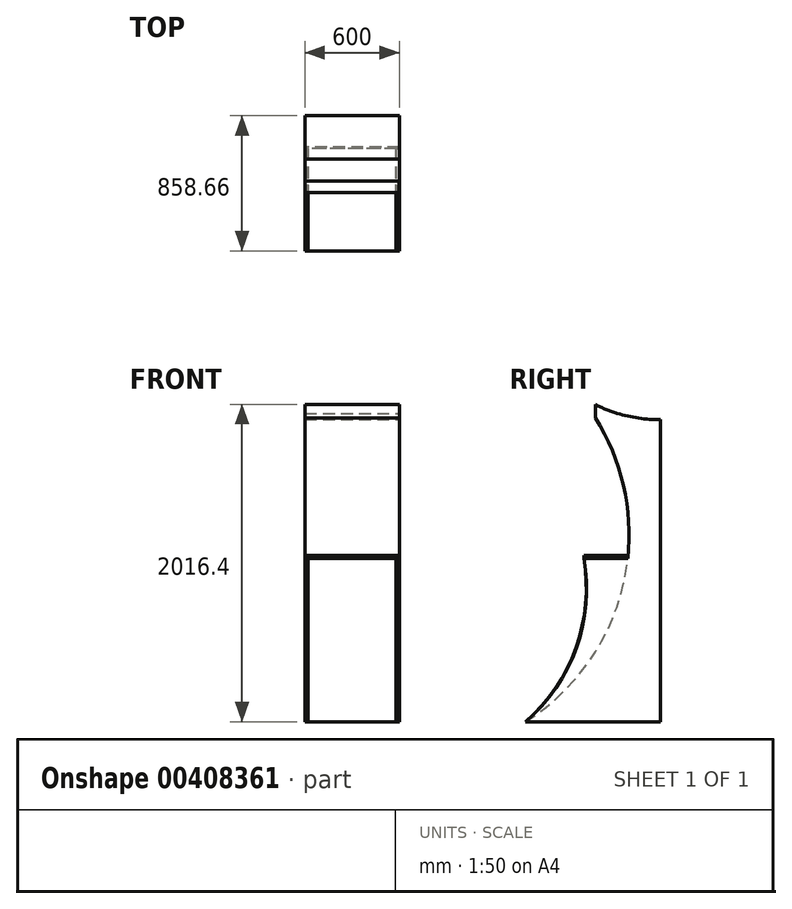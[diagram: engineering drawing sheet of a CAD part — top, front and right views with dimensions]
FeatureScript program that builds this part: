
annotation { "Feature Type Name" : "Feature", "Feature Type Description" : "" }
export const myFeature = defineFeature(function(context is Context, id is Id, definition is map)
    precondition{}
    {
        {
            var Q0;
            Q0=qCreatedBy(makeId("Right.planeOp"),FACE);
            var sketch = newSketch(context, id + "F0", { "sketchPlane" : qUnion([Q0])});
            skLineSegment(sketch, "E0", {"start": v(-858.66, 1.3) * mm, "end": v(841.34, 1.3) * mm});
            skPoint(sketch, "E1.end.orphan", {"position": v(0, 1171.1) * mm});
            skArc(sketch, "E2", {"start": v(-413.77, 2017.7) * mm, "mid": v(-217.07, 1948.77) * mm, "end": v(-8.66, 1951.3) * mm});
            skArc(sketch, "E3", {"start": v(-8.66, 1951.3) * mm, "mid": v(199.75, 1948.77) * mm, "end": v(396.44, 2017.7) * mm});
            skLineSegment(sketch, "E4", {"start": v(-413.77, 2017.7) * mm, "end": v(-413.77, 1932.7) * mm});
            skLineSegment(sketch, "E5", {"start": v(396.44, 2017.7) * mm, "end": v(396.44, 1932.7) * mm});
            skArc(sketch, "E6", {"start": v(-858.66, 1.3) * mm, "mid": v(-235.62, 874.72) * mm, "end": v(-413.77, 1932.7) * mm});
            skArc(sketch, "E7", {"start": v(396.44, 1932.7) * mm, "mid": v(218.29, 874.72) * mm, "end": v(841.34, 1.3) * mm});
            skPoint(sketch, "E8.start.orphan", {"position": v(-8.66, 1.3) * mm});
            skSolve(sketch);
        }
        {
            var Q0;
            Q0=makeQuery(id+"F0.imprint","IMPRINT",FACE,{"disambiguationData":[TD([[makeQuery(id+"F0.imprint","IMPRINT",EDGE,{"derivedFrom":sQuery(id+"F0.wireOp",EDGE,"E0")}),1.0]])]});
            extrude(context, id + "F1", {"entities" : qUnion([Q0]), "depth" : 600 * mm});
        }
        {
            var Q0;
            Q0=makeQuery(id+"F1.opExtrude","CAP_FACE",FACE,{"disambiguationData":[OSD([sQuery(id+"F0.wireOp",EDGE,"E0"),sQuery(id+"F0.wireOp",EDGE,"E2"),sQuery(id+"F0.wireOp",EDGE,"E3"),sQuery(id+"F0.wireOp",EDGE,"E4"),sQuery(id+"F0.wireOp",EDGE,"E5"),sQuery(id+"F0.wireOp",EDGE,"E6"),sQuery(id+"F0.wireOp",EDGE,"E7")])],"isStart":false});
            var sketch = newSketch(context, id + "F2", { "sketchPlane" : qUnion([Q0])});
            skArc(sketch, "E9", {"start": v(-413.77, 2017.7) * mm, "mid": v(-8.66, 1920.6) * mm, "end": v(396.44, 2017.7) * mm});
            skLineSegment(sketch, "E10", {"start": v(-413.77, 2017.7) * mm, "end": v(396.44, 2017.7) * mm});
            skSolve(sketch);
        }
        {
            var Q0;
            {var subQ0=sQuery(id+"F2.wireOp",EDGE,"E10");Q0=makeQuery(id+"F2.imprint","IMPRINT",FACE,{"disambiguationData":[TD([[makeQuery(id+"F2.imprint","IMPRINT",EDGE,{"derivedFrom":subQ0}),-1.0]])]});}
            var Q1;
            {var subQ0=sQuery(id+"F2.wireOp",EDGE,"E9");var subQ1=makeQuery(id+"F1.opExtrude","CAP_EDGE",EDGE,{"disambiguationData":[OSD([sQuery(id+"F0.wireOp",EDGE,"E2")])],"isStart":false});var subQ2=makeQuery(id+"F2.imprint","INTERSECT",VERTEX,{"derivedFrom":[subQ1,subQ0]});Q1=makeQuery(id+"F2.imprint","IMPRINT",FACE,{"disambiguationData":[TD([[makeQuery(id+"F2.imprint","IMPRINT",EDGE,{"disambiguationData":[TD([[subQ2,-1.0]])],"derivedFrom":subQ0}),1.0]])]});}
            extrude(context, id + "F3", {"entities" : qUnion([Q0, Q1]), "operationType" : NewBodyOperationType.REMOVE, "endBound" : BoundingType.THROUGH_ALL, "oppositeDirection" : true, "depth" : 25 * mm});
        }
        {
            var Q0;
            Q0=makeQuery(id+"F1.opExtrude","CAP_FACE",FACE,{"disambiguationData":[OSD([sQuery(id+"F0.wireOp",EDGE,"E0"),sQuery(id+"F0.wireOp",EDGE,"E2"),sQuery(id+"F0.wireOp",EDGE,"E3"),sQuery(id+"F0.wireOp",EDGE,"E4"),sQuery(id+"F0.wireOp",EDGE,"E5"),sQuery(id+"F0.wireOp",EDGE,"E6"),sQuery(id+"F0.wireOp",EDGE,"E7")])],"isStart":false});
            var sketch = newSketch(context, id + "F4", { "sketchPlane" : qUnion([Q0])});
            skArc(sketch, "E11", {"start": v(-858.66, 1.3) * mm, "mid": v(-533.5, 470.59) * mm, "end": v(-487.87, 1039.7) * mm});
            skLineSegment(sketch, "E12", {"start": v(-487.87, 1039.7) * mm, "end": v(-207.87, 1039.7) * mm});
            skLineSegment(sketch, "E13", {"start": v(190.54, 1039.7) * mm, "end": v(470.54, 1039.7) * mm});
            skArc(sketch, "E14", {"start": v(470.54, 1039.7) * mm, "mid": v(516.17, 470.59) * mm, "end": v(841.34, 1.3) * mm});
            skSolve(sketch);
        }
        {
            var Q0;
            {var subQ0=sQuery(id+"F4.wireOp",EDGE,"E11");Q0=makeQuery(id+"F4.imprint","IMPRINT",FACE,{"disambiguationData":[TD([[makeQuery(id+"F4.imprint","IMPRINT",EDGE,{"derivedFrom":subQ0}),-1.0]])]});}
            var Q1;
            {var subQ0=sQuery(id+"F4.wireOp",EDGE,"E13");Q1=makeQuery(id+"F4.imprint","IMPRINT",FACE,{"disambiguationData":[TD([[makeQuery(id+"F4.imprint","IMPRINT",EDGE,{"derivedFrom":subQ0}),-1.0]])]});}
            extrude(context, id + "F5", {"entities" : qUnion([Q0, Q1]), "operationType" : NewBodyOperationType.ADD, "oppositeDirection" : true, "depth" : 20 * mm});
        }
        {
            var Q0;
            Q0=makeQuery(id+"F1.opExtrude","CAP_FACE",FACE,{"disambiguationData":[OSD([sQuery(id+"F0.wireOp",EDGE,"E0"),sQuery(id+"F0.wireOp",EDGE,"E2"),sQuery(id+"F0.wireOp",EDGE,"E3"),sQuery(id+"F0.wireOp",EDGE,"E4"),sQuery(id+"F0.wireOp",EDGE,"E5"),sQuery(id+"F0.wireOp",EDGE,"E6"),sQuery(id+"F0.wireOp",EDGE,"E7")])],"isStart":true});
            var sketch = newSketch(context, id + "F6", { "sketchPlane" : qUnion([Q0])});
            skLineSegment(sketch, "E15", {"start": v(-190.65, 1038.7) * mm, "end": v(-470.65, 1038.7) * mm});
            skLineSegment(sketch, "E16", {"start": v(207.88, 1039.64) * mm, "end": v(487.88, 1039.64) * mm});
            skArc(sketch, "E17", {"start": v(-841.34, 1.3) * mm, "mid": v(-519.68, 471.3) * mm, "end": v(-470.65, 1038.7) * mm});
            skArc(sketch, "E18", {"start": v(487.88, 1039.64) * mm, "mid": v(536.71, 471.7) * mm, "end": v(858.66, 1.3) * mm});
            skSolve(sketch);
        }
        {
            var Q0;
            {var subQ0=sQuery(id+"F6.wireOp",EDGE,"E15");Q0=makeQuery(id+"F6.imprint","IMPRINT",FACE,{"disambiguationData":[TD([[makeQuery(id+"F6.imprint","IMPRINT",EDGE,{"derivedFrom":subQ0}),1.0]])]});}
            var Q1;
            {var subQ0=sQuery(id+"F6.wireOp",EDGE,"E16");Q1=makeQuery(id+"F6.imprint","IMPRINT",FACE,{"disambiguationData":[TD([[makeQuery(id+"F6.imprint","IMPRINT",EDGE,{"derivedFrom":subQ0}),-1.0]])]});}
            extrude(context, id + "F7", {"entities" : qUnion([Q0, Q1]), "operationType" : NewBodyOperationType.ADD, "oppositeDirection" : true, "depth" : 20 * mm});
        }
        {
            var Q0;
            Q0=makeQuery(id+"F7.opExtrude","SWEPT_FACE",FACE,{"disambiguationData":[OSD([sQuery(id+"F6.wireOp",EDGE,"E16")])]});
            var sketch = newSketch(context, id + "F8", { "sketchPlane" : qUnion([Q0])});
            skLineSegment(sketch, "E19", {"start": v(0, -487.88) * mm, "end": v(598.82, -487.88) * mm});
            skLineSegment(sketch, "E20", {"start": v(598.82, -487.88) * mm, "end": v(598.82, -209.16) * mm});
            skLineSegment(sketch, "E21", {"start": v(598.82, -209.16) * mm, "end": v(0, -209.16) * mm});
            skLineSegment(sketch, "E22", {"start": v(0, -209.16) * mm, "end": v(0, -487.88) * mm});
            skSolve(sketch);
        }
        {
            var Q0;
            {var subQ0=sQuery(id+"F8.wireOp",EDGE,"E22");Q0=makeQuery(id+"F8.imprint","IMPRINT",FACE,{"disambiguationData":[TD([[makeQuery(id+"F8.imprint","IMPRINT",EDGE,{"derivedFrom":subQ0}),1.0]])]});}
            var Q1;
            {var subQ3=sQuery(id+"F8.wireOp",EDGE,"E20");Q1=makeQuery(id+"F8.imprint","IMPRINT",FACE,{"disambiguationData":[TD([[makeQuery(id+"F8.imprint","IMPRINT",EDGE,{"derivedFrom":subQ3}),1.0]])]});}
            extrude(context, id + "F9", {"entities" : qUnion([Q0, Q1]), "operationType" : NewBodyOperationType.ADD, "depth" : 20 * mm});
        }
        {
            var Q0;
            Q0=qCreatedBy(makeId("Top.planeOp"),FACE);
            var sketch = newSketch(context, id + "F10", { "sketchPlane" : qUnion([Q0])});
            skLineSegment(sketch, "E23", {"start": v(0, 0) * mm, "end": v(0, -272.11) * mm});
            skLineSegment(sketch, "E24", {"start": v(0, -272.11) * mm, "end": v(598.53, -272.11) * mm});
            skLineSegment(sketch, "E25", {"start": v(598.53, -272.11) * mm, "end": v(598.53, 254.78) * mm});
            skLineSegment(sketch, "E26", {"start": v(598.53, 254.78) * mm, "end": v(0, 254.78) * mm});
            skLineSegment(sketch, "E27", {"start": v(0, 254.78) * mm, "end": v(0, 0) * mm});
            skLineSegment(sketch, "E28", {"start": v(598.53, 0) * mm, "end": v(0, 0) * mm});
            skLineSegment(sketch, "E29", {"start": v(0, 0) * mm, "end": v(0, 963.85) * mm});
            skPoint(sketch, "E29.endSnap0", {"position": v(0, 127.4) * mm});
            skLineSegment(sketch, "E30", {"start": v(0, 963.85) * mm, "end": v(664.88, 963.85) * mm});
            skLineSegment(sketch, "E31", {"start": v(664.88, 963.85) * mm, "end": v(664.88, 0) * mm});
            skLineSegment(sketch, "E32", {"start": v(664.88, 0) * mm, "end": v(-87.83, 0) * mm});
            skLineSegment(sketch, "E33", {"start": v(-87.83, 0) * mm, "end": v(-87.83, 963.85) * mm});
            skLineSegment(sketch, "E34", {"start": v(-87.83, 963.85) * mm, "end": v(0, 963.85) * mm});
            skSolve(sketch);
        }
        {
            var Q0;
            {var subQ2=sQuery(id+"F10.wireOp",EDGE,"E26");Q0=makeQuery(id+"F10.imprint","IMPRINT",FACE,{"disambiguationData":[TD([[makeQuery(id+"F10.imprint","IMPRINT",EDGE,{"derivedFrom":subQ2}),-1.0]])]});}
            var Q1;
            {var subQ0=sQuery(id+"F10.wireOp",EDGE,"E33");Q1=makeQuery(id+"F10.imprint","IMPRINT",FACE,{"disambiguationData":[TD([[makeQuery(id+"F10.imprint","IMPRINT",EDGE,{"derivedFrom":subQ0}),-1.0]])]});}
            var Q2;
            {var subQ0=sQuery(id+"F10.wireOp",EDGE,"E26");Q2=makeQuery(id+"F10.imprint","IMPRINT",FACE,{"disambiguationData":[TD([[makeQuery(id+"F10.imprint","IMPRINT",EDGE,{"derivedFrom":subQ0}),1.0]])]});}
            var Q3;
            Q3=makeQuery(id+"F8rLvzEEGZTeDDi_1.opExtrude","CAP_FACE",FACE,{"disambiguationData":[OSD([sQuery(id+"F4.wireOp",EDGE,"E13"),sQuery(id+"FjRxR3VPPXWF50J_1.wireOp",EDGE,"HHmMcipD-GxRH-TbMR-t4Jx-SAwCge4ooCil"),sQuery(id+"FjRxR3VPPXWF50J_1.wireOp",EDGE,"RKBa9ipd-hSD7-eZ8H-kpQ8-cLbgrZFbzUEb"),sQuery(id+"FjRxR3VPPXWF50J_1.wireOp",EDGE,"qFZhktBO-3kNu-xGq9-FTlY-OW7O7ifnl3fo")])],"isStart":true});
            extrude(context, id + "F11", {"entities" : qUnion([Q0, Q1, Q2, Q3]), "operationType" : NewBodyOperationType.REMOVE, "endBound" : BoundingType.THROUGH_ALL, "depth" : 25 * mm});
        }
    });
